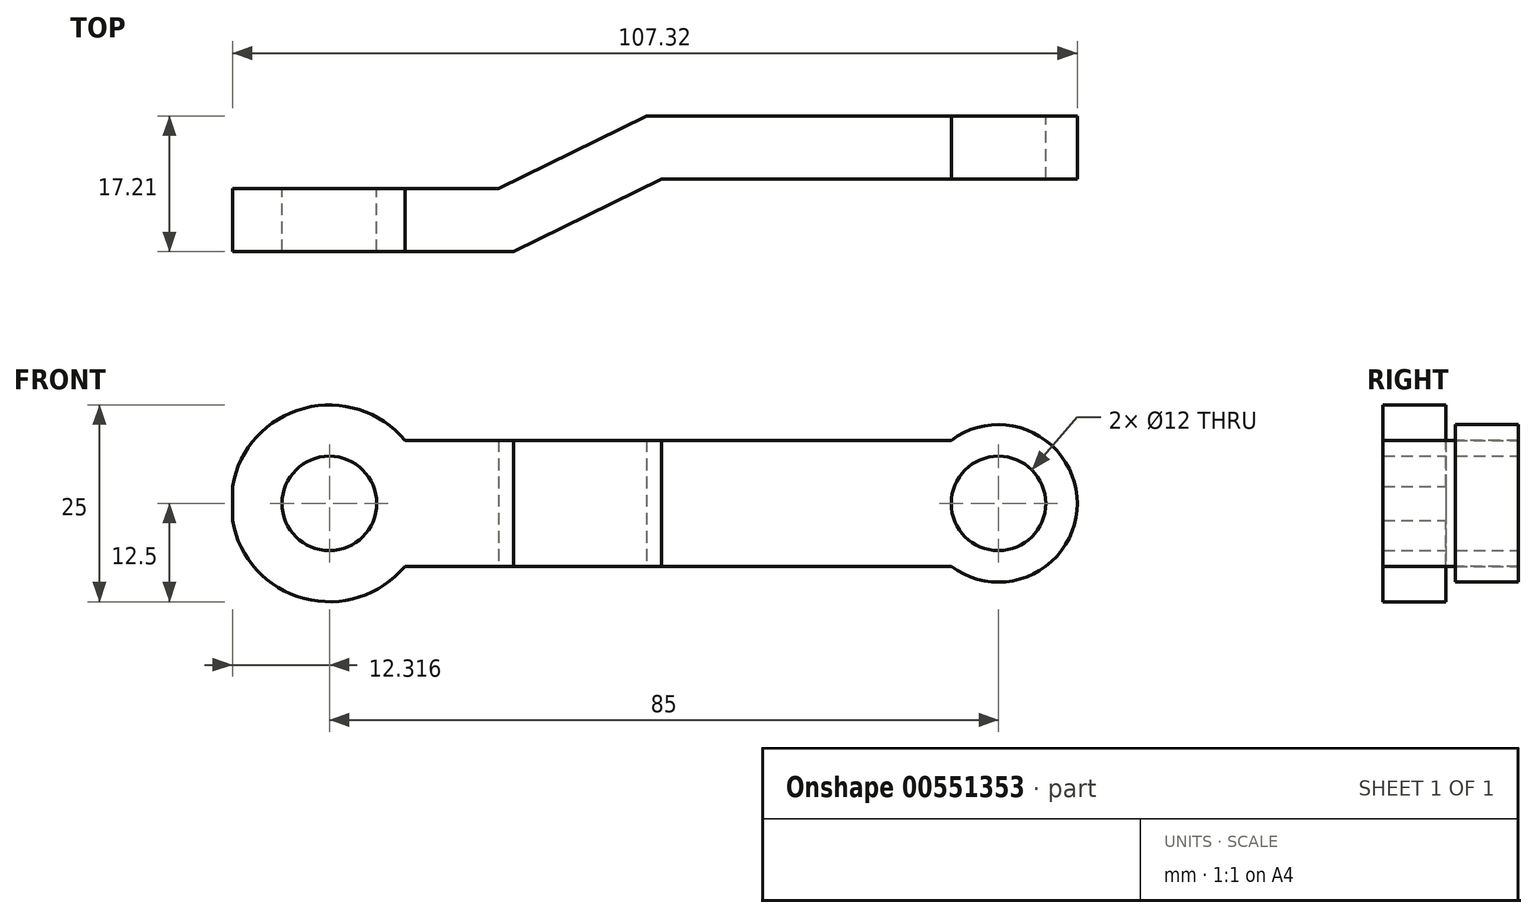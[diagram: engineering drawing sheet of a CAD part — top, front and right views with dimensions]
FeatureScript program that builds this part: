
annotation { "Feature Type Name" : "Feature", "Feature Type Description" : "" }
export const myFeature = defineFeature(function(context is Context, id is Id, definition is map)
    precondition{}
    {
        {
            var Q0;
            Q0=qCreatedBy(makeId("Front.planeOp"),FACE);
            var sketch = newSketch(context, id + "F0", { "sketchPlane" : qUnion([Q0])});
            skCircle(sketch, "E0", {"center": v(-40.31, 0) * mm, "radius": 12.5 * mm});
            skCircle(sketch, "E1", {"center": v(44.69, 0) * mm, "radius": 10 * mm});
            skLineSegment(sketch, "E2", {"start": v(-30.7, 8) * mm, "end": v(38.69, 8) * mm});
            skLineSegment(sketch, "E3.MirrorCS", {"start": v(-30.7, -8) * mm, "end": v(38.69, -8) * mm});
            skCircle(sketch, "E4", {"center": v(-40.31, 0) * mm, "radius": 6 * mm});
            skCircle(sketch, "E5", {"center": v(44.69, 0) * mm, "radius": 6 * mm});
            skSolve(sketch);
        }
        {
            var Q0;
            Q0=makeQuery(id+"F0.imprint","IMPRINT",FACE,{"disambiguationData":[TD([[makeQuery(id+"F0.imprint","IMPRINT",EDGE,{"derivedFrom":sQuery(id+"F0.wireOp",EDGE,"E4")}),-1.0]])]});
            var Q1;
            {var subQ0=sQuery(id+"F0.wireOp",EDGE,"E2");Q1=makeQuery(id+"F0.imprint","IMPRINT",FACE,{"disambiguationData":[TD([[makeQuery(id+"F0.imprint","IMPRINT",EDGE,{"derivedFrom":subQ0}),-1.0]])]});}
            var Q2;
            Q2=makeQuery(id+"F0.imprint","IMPRINT",FACE,{"disambiguationData":[TD([[makeQuery(id+"F0.imprint","IMPRINT",EDGE,{"derivedFrom":sQuery(id+"F0.wireOp",EDGE,"E5")}),-1.0]])]});
            extrude(context, id + "F1", {"entities" : qUnion([Q0, Q1, Q2]), "depth" : 25 * mm, "offsetDistance" : 25 * mm});
        }
        {
            var Q0;
            Q0=qCreatedBy(makeId("Top.planeOp"),FACE);
            var sketch = newSketch(context, id + "F2", { "sketchPlane" : qUnion([Q0])});
            skLineSegment(sketch, "E6", {"start": v(-52.63, -9.2) * mm, "end": v(-18.8, -9.2) * mm});
            skLineSegment(sketch, "E7", {"start": v(-18.8, -9.2) * mm, "end": v(0, 0) * mm});
            skLineSegment(sketch, "E8", {"start": v(0, 0) * mm, "end": v(55.07, 0) * mm});
            skLineSegment(sketch, "E9.0", {"start": v(1.85, -8) * mm, "end": v(55.07, -8) * mm});
            skLineSegment(sketch, "E9.1", {"start": v(-16.94, -17.2) * mm, "end": v(1.85, -8) * mm});
            skLineSegment(sketch, "E9.2", {"start": v(-52.63, -17.2) * mm, "end": v(-16.94, -17.2) * mm});
            skLineSegment(sketch, "E10", {"start": v(-52.63, -9.2) * mm, "end": v(-52.63, -17.2) * mm});
            skLineSegment(sketch, "E11", {"start": v(55.07, 0) * mm, "end": v(55.07, -8) * mm});
            skSolve(sketch);
        }
        {
            var Q0;
            Q0=makeQuery(id+"F2.imprint","IMPRINT",FACE,{"disambiguationData":[TD([[makeQuery(id+"F2.imprint","IMPRINT",EDGE,{"derivedFrom":sQuery(id+"F2.wireOp",EDGE,"E6")}),-1.0]])]});
            var Q1;
            Q1=sQuery(id+"F2.wireOp",EDGE,"E9.1");
            var Q2;
            Q2=sQuery(id+"F2.wireOp",EDGE,"E9.2");
            var Q3;
            Q3=sQuery(id+"F2.wireOp",EDGE,"E10");
            var Q4;
            Q4=sQuery(id+"F2.wireOp",EDGE,"E7");
            var Q5;
            Q5=sQuery(id+"F2.wireOp",EDGE,"E6");
            var Q6;
            Q6=sQuery(id+"F2.wireOp",EDGE,"E8");
            var Q7;
            Q7=sQuery(id+"F2.wireOp",EDGE,"E9.0");
            var Q8;
            Q8=sQuery(id+"F2.wireOp",EDGE,"E11");
            extrude(context, id + "F3", {"entities" : qUnion([Q0]), "operationType" : NewBodyOperationType.INTERSECT, "surfaceEntities" : qUnion([Q1, Q2, Q3, Q4, Q5, Q6, Q7, Q8]), "endBound" : BoundingType.SYMMETRIC, "depth" : 25 * mm, "offsetDistance" : 25 * mm});
        }
    });
